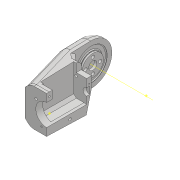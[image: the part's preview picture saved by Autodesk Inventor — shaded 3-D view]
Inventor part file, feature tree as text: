
AUTODESK INVENTOR PART (.ipt)
format: ipt  version: 2018 (Build 220112000, 112)  size: 1,025,536 bytes
history: native  units: mm
features: projected_geometry x49, sketch x47, extrude x39, hole x13, fillet x12, other x10, chamfer x6, reference x3, mirror x1, plane x1
ambient origin geometry x8: Origin, YZ Plane, XZ Plane, XY Plane, X Axis, Y Axis, Z Axis, Center Point
bodies: Solid1 (feature_tree)
feature tree (181):
  extrude  "Extrusion1"  Depth=45.0mm
  extrude  "Extrusion2"  Depth=2.25mm
  hole  "Hole1"  [1 undecoded]
  hole  "Hole2"  [1 undecoded]
  fillet  "Fillet1"  Radius=14.0mm
  extrude  "Extrusion3"  Depth=18.5mm
  extrude  "Extrusion4"  Depth=10.0mm
  extrude  "Extrusion5"  Depth=2.0mm
  extrude  "Extrusion6"  Depth=8.0mm
  hole  "Hole3"  [1 undecoded]
  extrude  "Extrusion7"  Depth=0.5mm
  extrude  "Extrusion8"  Depth=1.0mm TaperAngle=0.0deg
  extrude  "Extrusion9"  Depth=24.5mm
  extrude  "Extrusion10"  Depth=10.0mm
  extrude  "Extrusion11"  Depth=14.5mm
  extrude  "Extrusion13"  Depth=14.5mm
  extrude  "Extrusion14"  Depth=5.0mm
  extrude  "Extrusion15"  Depth=2.25mm
  extrude  "Extrusion16"  Depth=5.0mm
  extrude  "Extrusion17"  Depth=9.0mm
  chamfer  "Chamfer1"  Distance=1.0mm
  fillet  "Fillet7"  Radius=20.7mm
  fillet  "Fillet8"  Radius=32.0mm
  mirror  "Mirror1"
  sketch  "Sketch26"  dims[d55=2.25mm d56=5.0mm]
  extrude  "Extrusion24"  Depth=1.0mm TaperAngle=0.0deg
  extrude  "Extrusion25"  Depth=8.0mm
  extrude  "Extrusion26"  Depth=0.2mm TaperAngle=0.0deg
  extrude  "Extrusion27"  Depth=8.0mm TaperAngle=0.0deg
  other  "Work Axis1"
  plane  "Work Plane2"
  extrude  "Extrusion28"  Depth=0.2mm TaperAngle=0.0deg
  extrude  "Extrusion29"  Depth=2.5mm TaperAngle=45.0deg
  extrude  "Extrusion31"  Depth=0.5mm
  extrude  "Extrusion32"  Depth=36.0mm
  extrude  "Extrusion33"  Depth=60.0mm
  sketch  "Sketch41"  dims[d100=0.2mm d101=0.0mm d102=2.5mm d103=2.0mm d104=45.0deg]
  extrude  "Extrusion34"  Depth=2.3mm
  chamfer  "Chamfer6"  Distance=15.0mm
  fillet  "Fillet9"  Radius=15.0mm
  extrude  "Extrusion35"  Depth=15.0mm TaperAngle=0.0deg
  extrude  "Extrusion36"  Depth=41.5mm
  fillet  "Fillet10"  Radius=15.5mm
  extrude  "Extrusion37"  Depth=5.0mm
  extrude  "Extrusion38"  Depth=100.0mm TaperAngle=0.0deg
  extrude  "Extrusion39"  Depth=11.5mm
  extrude  "Extrusion40"  Depth=11.5mm
  hole  "Hole6"  [1 undecoded]
  fillet  "Fillet12"  Radius=100.0mm
  extrude  "Extrusion41"  Depth=100.0mm TaperAngle=0.0deg
  extrude  "Extrusion42"  Depth=8.0mm
  hole  "Hole7"  [1 undecoded]
  extrude  "Extrusion43"  Depth=1.0mm TaperAngle=0.0deg
  extrude  "Extrusion44"  Depth=2.0mm
  sketch  "Sketch58"  dims[d202=15.0deg d204=10.970628mm]
  hole  "Hole8"  [1 undecoded]
  hole  "Hole9"  [1 undecoded]
  hole  "Hole10"  [1 undecoded]
  hole  "Hole11"  [1 undecoded]
  hole  "Hole12"  [1 undecoded]
  hole  "Hole13"  [1 undecoded]
  hole  "Hole14"  [1 undecoded]
  hole  "Hole15"  [1 undecoded]
  chamfer  "Chamfer10"  Distance=20.5mm
  chamfer  "Chamfer11"  Distance=3.05mm
  chamfer  "Chamfer12"  Distance=14.0mm
  chamfer  "Chamfer13"  Distance=20.5mm
  extrude  "Extrusion45"  Depth=1.55mm TaperAngle=0.0deg
  fillet  "Fillet13"  Radius=8.0mm
  extrude  "Extrusion46"  Depth=2.5mm TaperAngle=0.0deg
  fillet  "Fillet14"  Radius=8.0mm
  fillet  "Fillet15"  Radius=2.5mm
  fillet  "Fillet16"  Radius=4.624622mm
  fillet  "Fillet17"  Radius=4.624622mm
  fillet  "Fillet18"  Radius=2.75mm
  extrude  "Extrusion47"  Depth=2.75mm
  sketch  "Sketch1"  dims[d0=24.5mm d1=45.0mm]
  sketch  "Sketch2"  dims[d2=1.95mm d3=0.0mm d4=2.25mm]
  projected_geometry  "Projected Loop1"
  sketch  "Sketch3"  dims[d5=20.0mm d6=2.25mm]
  projected_geometry  "Projected Loop2"
  sketch  "Sketch4"  dims[d7=5.25mm d8=5.25mm d9=14.0mm]
  projected_geometry  "Projected Loop3"
  sketch  "Sketch5"  dims[d10=5.25mm d11=18.5mm]
  projected_geometry  "Projected Loop4"
  sketch  "Sketch6"  dims[d12=10.0mm d13=0.0mm d14=20.5mm]
  projected_geometry  "Projected Loop5"
  sketch  "Sketch7"  dims[d15=2.0mm d16=2.195mm]
  projected_geometry  "Projected Loop6"
  sketch  "Sketch8"  dims[d17=2.0mm]
  projected_geometry  "Projected Loop7"
  sketch  "Sketch9"  dims[d18=2.4mm d19=6.0mm d20=4.4mm d21=2.0mm d22=90.0deg d23=8.0mm d24=20.594885mm d25=20.5mm]
  projected_geometry  "Projected Loop8"
  projected_geometry  "Projected Loop9"
  sketch  "Sketch10"  dims[d26=26.65mm d27=2.0mm]
  projected_geometry  "Projected Loop10"
  projected_geometry  "Projected Loop11"
  sketch  "Sketch11"  dims[d28=2.0mm]
  projected_geometry  "Projected Loop12"
  sketch  "Sketch12"  dims[d29=2.4mm d30=6.0mm d31=4.4mm d32=2.0mm d33=90.0deg d34=8.0mm d35=20.594885mm d36=0.5mm]
  sketch  "Sketch13"  dims[d37=18.0mm d38=1.0mm d39=0.0mm]
  sketch  "Sketch14"  dims[d41=5.0mm d42=0.0mm d43=24.5mm]
  projected_geometry  "Projected Loop13"
  sketch  "Sketch16"  dims[d44=1.15mm d45=0.0mm d46=10.0mm]
  projected_geometry  "Projected Loop14"
  sketch  "Sketch17"  dims[d47=21.0mm d48=14.5mm]
  projected_geometry  "Projected Loop15"
  sketch  "Sketch18"  dims[d49=20.0mm d50=14.5mm]
  projected_geometry  "Projected Loop16"
  sketch  "Sketch19"  dims[d51=24.5mm d52=5.0mm]
  projected_geometry  "Projected Loop17"
  sketch  "Sketch20"  dims[d53=5.0mm d54=2.25mm]
  projected_geometry  "Projected Loop18"
  projected_geometry  "Projected Loop25"
  sketch  "Sketch31"  dims[d57=5.0mm d58=9.0mm]
  projected_geometry  "Projected Loop30"
  reference  "Reference1"
  sketch  "Sketch32"  dims[d59=14.75mm]
  projected_geometry  "Projected Loop31"
  sketch  "Sketch33"  dims[d60=4.0mm d61=1.0mm d62=0.0mm d63=20.7mm]
  projected_geometry  "Projected Loop32"
  sketch  "Sketch34"  dims[d64=2.3mm d65=6.0mm d66=4.4mm d67=2.0mm d68=90.0deg d69=8.0mm d70=20.594885mm d72=32.0mm]
  projected_geometry  "Projected Loop33"
  other  "Work Point1"
  other  "Work Point2"
  other  "Work Point3"
  sketch  "Sketch35"  dims[d73=3.0mm d74=0.0mm d75=1.0mm d76=0.0mm]
  sketch  "Sketch37"  dims[d77=12.25mm d78=0.0mm d80=8.0mm]
  projected_geometry  "Projected Loop34"
  sketch  "Sketch38"  dims[d81=4.5mm d82=0.0mm d84=0.2mm d85=0.0mm]
  sketch  "Sketch39"  dims[d91=8.0mm d92=0.0mm d93=5.0mm d94=0.0mm]
  sketch  "Sketch40"  dims[d95=5.0mm d96=0.0mm d98=0.2mm d99=0.0mm]
  projected_geometry  "Projected Loop35"
  projected_geometry  "Projected Loop36"
  projected_geometry  "Projected Loop37"
  projected_geometry  "Projected Loop38"
  sketch  "Sketch42"  dims[d105=1.5mm d114=0.5mm]
  projected_geometry  "Projected Loop39"
  sketch  "Sketch43"  dims[d130=60.0mm d131=36.0mm]
  reference  "Reference2"
  reference  "Reference3"
  sketch  "Sketch45"  dims[d146=40.0mm d147=60.0mm]
  projected_geometry  "Projected Loop40"
  sketch  "Sketch46"  dims[d148=0.0mm d149=2.3mm d150=15.0mm d151=0.0mm d152=15.0mm d153=0.0mm]
  projected_geometry  "Projected Loop41"
  sketch  "Sketch48"  dims[d154=15.0mm d155=0.0mm d156=15.0mm d157=0.0mm]
  projected_geometry  "Projected Loop43"
  sketch  "Sketch49"  dims[d158=20.5mm d159=41.5mm d160=15.5mm]
  projected_geometry  "Projected Loop44"
  projected_geometry  "Projected Loop45"
  sketch  "Sketch50"  dims[d161=15.5mm d162=5.0mm]
  projected_geometry  "Projected Loop46"
  sketch  "Sketch52"  dims[d165=100.0mm d166=0.0mm d167=100.0mm d168=0.0mm]
  sketch  "Sketch53"  dims[d172=0.0mm d173=11.5mm]
  projected_geometry  "Projected Loop47"
  sketch  "Sketch54"  dims[d175=11.5mm d176=11.5mm]
  projected_geometry  "Projected Loop48"
  sketch  "Sketch55"  dims[d179=100.0mm d180=0.0mm d187=7.0mm d188=100.0mm d189=0.0mm]
  sketch  "Sketch56"  dims[d193=100.0mm d194=0.0mm d195=100.0mm d196=0.0mm]
  projected_geometry  "Projected Loop49"
  sketch  "Sketch57"  dims[d197=5.0mm d198=2.0mm d199=45.0deg d200=8.0mm]
  projected_geometry  "Projected Loop50"
  projected_geometry  "Projected Loop51"
  projected_geometry  "Projected Loop52"
  projected_geometry  "Projected Loop53"
  projected_geometry  "Projected Loop55"
  projected_geometry  "Projected Loop56"
  projected_geometry  "Projected Loop57"
  sketch  "Sketch59"  dims[d205=15.470628mm d206=1.0mm d207=0.0mm]
  projected_geometry  "Projected Loop58"
  sketch  "Sketch60"  dims[d208=1.0mm d209=0.0mm d213=2.0mm]
  projected_geometry  "Projected Loop59"
  sketch  "Sketch61"  dims[d215=15.0deg d216=4.0mm d217=4.0mm d218=5.0mm d219=0.0mm d222=32.0mm d223=4.0mm d224=0.0mm d225=2.5mm d226=0.0mm d227=6.5mm d228=0.0mm d235=1.567mm d236=15.0mm d237=4.0mm d238=2.0mm d239=90.0deg d240=15.0mm d241=20.594885mm d243=0.75mm d244=20.5mm d245=3.05mm d246=0.0mm d247=14.0mm d248=3.2mm d249=6.0mm d250=4.0mm d251=2.0mm d252=90.0deg d253=8.8mm d254=20.594885mm d255=20.5mm d256=1.55mm d257=0.0mm d258=8.0mm d259=2.5mm d260=0.0mm d261=8.0mm d262=2.5mm d263=0.0mm d266=4.624622mm d267=4.624622mm d268=2.75mm d269=2.75mm d270=2.35mm d271=2.35mm d272=14.0mm d273=4.0mm d274=5.6mm d275=3.708mm d276=3.023mm d277=2.0mm d278=14.3117mm d279=17.0mm d280=0.0mm d281=4.0mm d282=3.708mm d283=3.023mm d284=2.0mm d285=14.3117mm d286=19.0mm d287=0.0mm d288=4.0mm d289=3.708mm d290=3.023mm d291=2.0mm d292=14.3117mm d293=20.0mm d294=0.0mm d295=2.3mm d296=4.0mm d297=4.4mm d298=2.0mm d299=90.0deg d300=32.25mm d301=0.0mm d302=3.3mm d303=4.0mm d304=6.3mm d305=2.0mm d306=90.0deg d307=32.25mm d308=0.0mm d309=1.567mm d310=4.0mm d311=6.3mm d312=2.0mm d313=90.0deg d314=45.0mm d315=20.594885mm d316=1.567mm d317=4.0mm d318=6.3mm d319=2.0mm d320=90.0deg d321=55.0mm d322=20.594885mm d323=2.459mm d324=6.0mm d325=6.3mm d326=2.0mm d327=90.0deg d328=50.0mm d329=20.594885mm d330=3.0mm d331=2.0mm d332=45.0deg d333=5.0mm d334=20.0mm d335=45.0deg d336=5.0mm d337=20.0mm d338=45.0deg d339=5.0mm d340=20.0mm d341=45.0deg d342=6.0mm d343=6.0mm d344=6.0mm d345=6.0mm d346=2.0mm d347=0.0mm d348=1.5mm d349=6.0mm d350=6.0mm d351=6.0mm d352=6.0mm d353=3.0mm d354=0.0mm d355=1.5mm d356=0.4mm d357=0.4mm d358=0.3mm d359=1.0mm d360=0.6mm d361=32.25mm d362=0.0mm]
  parser-record x1  (decoder bookkeeping rows leaked as tree rows — omitted from the tree; the rows remain in map.json)
  other  "servocheck.iam"
  other  "LX-16A:3"
  other  "DUOPAN-SG-SJ_10"
  projected_geometry  "Project Cut Edges1"
  projected_geometry  "Project Cut Edges3"
  other  "bottomarm:1"
  other  "arm1:1"
note: 13 required parameter values undecoded (feature->parameter linkage not recoverable at this tier; creation-order binding heuristic only, values carry confidence <= 0.55)
note: 1 file-system path scrubbed to <path> (originals preserved in map.json)
